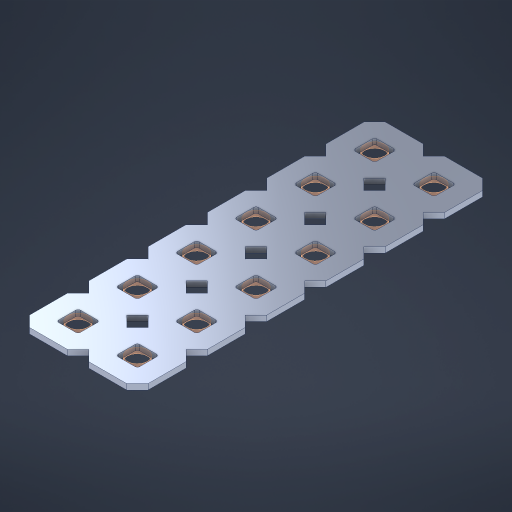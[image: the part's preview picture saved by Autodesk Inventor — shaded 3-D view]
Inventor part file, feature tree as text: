
AUTODESK INVENTOR PART (.ipt)
format: ipt  version: 2023 (Build 270158000, 158)  size: 384,512 bytes
history: native  units: in
note: dims shown in document units (in); Inventor stores cm internally (conversion verified against a paired STEP export)
features: other x13, extrude x11, sketch x2, pattern_linear x1
ambient origin geometry x8: Origin, YZ Plane, XZ Plane, XY Plane, X Axis, Y Axis, Z Axis, Center Point
bodies: Solid1 (feature_tree), Body (feature_tree)
feature tree (27):
  pattern_linear  "Rectangular Pattern1"  Spacing1=0.09in  [1 undecoded]
  sketch  "Sketch1"  dims[d1=0.5in]
  sketch  "Sketch2"  dims[d2=0.182in d3=0.09in d4=0.09in d5=0.09in d6=0.09in d7=0.09in d8=0.09in d9=0.09in d10=0.09in d11=0.02in d13=0.0in d14=0.172in d15=0.0625in d16=0.0in d19=0.5in d22=0.5in]
  other  "Srf1"
  other  "Srf126"
  other  "Srf127"
  other  "Srf128"
  other  "Srf129"
  other  "Srf130"
  other  "Srf268"
  other  "Srf269"
  other  "Srf270"
  other  "Srf271"
  other  "Srf272"
  other  "Srf273"
  other  "Circle"
  extrude  "ExtrusionSrf126"  Depth=0.09in
  extrude  "ExtrusionSrf127"  Depth=0.09in
  extrude  "ExtrusionSrf128"  Depth=0.09in
  extrude  "ExtrusionSrf129"  Depth=0.09in
  extrude  "ExtrusionSrf130"  Depth=0.09in
  extrude  "ExtrusionSrf268"  Depth=0.09in
  extrude  "ExtrusionSrf269"  Depth=0.09in
  extrude  "ExtrusionSrf270"  Depth=0.02in
  extrude  "ExtrusionSrf271"  TaperAngle=0.0deg  [1 undecoded]
  extrude  "ExtrusionSrf272"  Depth=0.5in
  extrude  "ExtrusionSrf273"  Depth=0.5in TaperAngle=0.0deg
note: 2 required parameter values undecoded (feature->parameter linkage not recoverable at this tier; creation-order binding heuristic only, values carry confidence <= 0.55)
